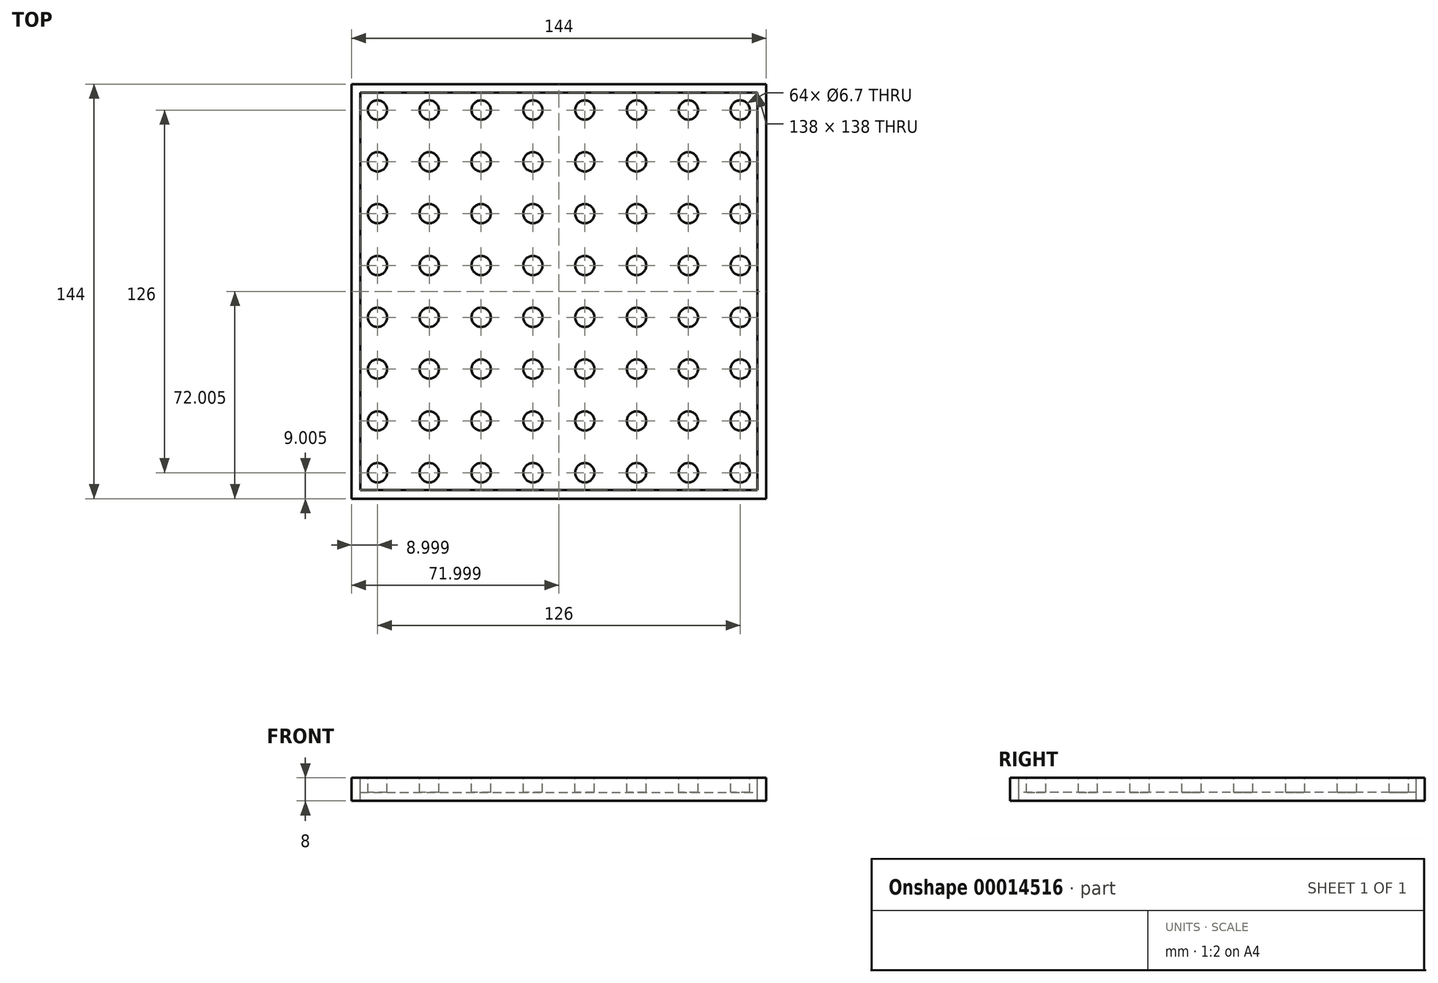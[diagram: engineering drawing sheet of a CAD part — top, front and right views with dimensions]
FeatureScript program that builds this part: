
annotation { "Feature Type Name" : "Feature", "Feature Type Description" : "" }
export const myFeature = defineFeature(function(context is Context, id is Id, definition is map)
    precondition{}
    {
        {
            var Q0;
            Q0=qCreatedBy(makeId("Top.planeOp"),FACE);
            var sketch = newSketch(context, id + "F0", { "sketchPlane" : qUnion([Q0])});
            skLineSegment(sketch, "E0.bottom", {"start": v(-70.46, 51.71) * mm, "end": v(73.54, 51.71) * mm});
            skLineSegment(sketch, "E0.top", {"start": v(-70.46, -92.29) * mm, "end": v(73.54, -92.29) * mm});
            skLineSegment(sketch, "E0.left", {"start": v(-70.46, 51.71) * mm, "end": v(-70.46, -92.29) * mm});
            skLineSegment(sketch, "E0.right", {"start": v(73.54, 51.71) * mm, "end": v(73.54, -92.29) * mm});
            skLineSegment(sketch, "E1.0", {"start": v(-67.46, 48.71) * mm, "end": v(70.54, 48.71) * mm});
            skLineSegment(sketch, "E1.1", {"start": v(-67.46, 48.71) * mm, "end": v(-67.46, -89.29) * mm});
            skLineSegment(sketch, "E1.2", {"start": v(-67.46, -89.29) * mm, "end": v(70.54, -89.29) * mm});
            skLineSegment(sketch, "E1.3", {"start": v(70.54, 48.71) * mm, "end": v(70.54, -89.29) * mm});
            skCircle(sketch, "E2", {"center": v(-61.46, 42.71) * mm, "radius": 3.35 * mm});
            skCircle(sketch, "E3.0.1.0", {"center": v(-61.46, 24.71) * mm, "radius": 3.35 * mm});
            skCircle(sketch, "E3.0.2.0", {"center": v(-61.46, 6.71) * mm, "radius": 3.35 * mm});
            skCircle(sketch, "E3.0.3.0", {"center": v(-61.46, -11.29) * mm, "radius": 3.35 * mm});
            skCircle(sketch, "E3.0.4.0", {"center": v(-61.46, -29.29) * mm, "radius": 3.35 * mm});
            skCircle(sketch, "E3.0.5.0", {"center": v(-61.46, -47.29) * mm, "radius": 3.35 * mm});
            skCircle(sketch, "E3.0.6.0", {"center": v(-61.46, -65.29) * mm, "radius": 3.35 * mm});
            skCircle(sketch, "E3.1.0.0", {"center": v(-43.46, 42.71) * mm, "radius": 3.35 * mm});
            skCircle(sketch, "E3.1.1.0", {"center": v(-43.46, 24.71) * mm, "radius": 3.35 * mm});
            skCircle(sketch, "E3.1.2.0", {"center": v(-43.46, 6.71) * mm, "radius": 3.35 * mm});
            skCircle(sketch, "E3.1.3.0", {"center": v(-43.46, -11.29) * mm, "radius": 3.35 * mm});
            skCircle(sketch, "E3.1.4.0", {"center": v(-43.46, -29.29) * mm, "radius": 3.35 * mm});
            skCircle(sketch, "E3.1.5.0", {"center": v(-43.46, -47.29) * mm, "radius": 3.35 * mm});
            skCircle(sketch, "E3.1.6.0", {"center": v(-43.46, -65.29) * mm, "radius": 3.35 * mm});
            skCircle(sketch, "E3.2.0.0", {"center": v(-25.46, 42.71) * mm, "radius": 3.35 * mm});
            skCircle(sketch, "E3.2.1.0", {"center": v(-25.46, 24.71) * mm, "radius": 3.35 * mm});
            skCircle(sketch, "E3.2.2.0", {"center": v(-25.46, 6.71) * mm, "radius": 3.35 * mm});
            skCircle(sketch, "E3.2.3.0", {"center": v(-25.46, -11.29) * mm, "radius": 3.35 * mm});
            skCircle(sketch, "E3.2.4.0", {"center": v(-25.46, -29.29) * mm, "radius": 3.35 * mm});
            skCircle(sketch, "E3.2.5.0", {"center": v(-25.46, -47.29) * mm, "radius": 3.35 * mm});
            skCircle(sketch, "E3.2.6.0", {"center": v(-25.46, -65.29) * mm, "radius": 3.35 * mm});
            skCircle(sketch, "E3.3.0.0", {"center": v(-7.46, 42.71) * mm, "radius": 3.35 * mm});
            skCircle(sketch, "E3.3.1.0", {"center": v(-7.46, 24.71) * mm, "radius": 3.35 * mm});
            skCircle(sketch, "E3.3.2.0", {"center": v(-7.46, 6.71) * mm, "radius": 3.35 * mm});
            skCircle(sketch, "E3.3.3.0", {"center": v(-7.46, -11.29) * mm, "radius": 3.35 * mm});
            skCircle(sketch, "E3.3.4.0", {"center": v(-7.46, -29.29) * mm, "radius": 3.35 * mm});
            skCircle(sketch, "E3.3.5.0", {"center": v(-7.46, -47.29) * mm, "radius": 3.35 * mm});
            skCircle(sketch, "E3.3.6.0", {"center": v(-7.46, -65.29) * mm, "radius": 3.35 * mm});
            skCircle(sketch, "E3.4.0.0", {"center": v(10.54, 42.71) * mm, "radius": 3.35 * mm});
            skCircle(sketch, "E3.4.1.0", {"center": v(10.54, 24.71) * mm, "radius": 3.35 * mm});
            skCircle(sketch, "E3.4.2.0", {"center": v(10.54, 6.71) * mm, "radius": 3.35 * mm});
            skCircle(sketch, "E3.4.3.0", {"center": v(10.54, -11.29) * mm, "radius": 3.35 * mm});
            skCircle(sketch, "E3.4.4.0", {"center": v(10.54, -29.29) * mm, "radius": 3.35 * mm});
            skCircle(sketch, "E3.4.5.0", {"center": v(10.54, -47.29) * mm, "radius": 3.35 * mm});
            skCircle(sketch, "E3.4.6.0", {"center": v(10.54, -65.29) * mm, "radius": 3.35 * mm});
            skCircle(sketch, "E3.5.0.0", {"center": v(28.54, 42.71) * mm, "radius": 3.35 * mm});
            skCircle(sketch, "E3.5.1.0", {"center": v(28.54, 24.71) * mm, "radius": 3.35 * mm});
            skCircle(sketch, "E3.5.2.0", {"center": v(28.54, 6.71) * mm, "radius": 3.35 * mm});
            skCircle(sketch, "E3.5.3.0", {"center": v(28.54, -11.29) * mm, "radius": 3.35 * mm});
            skCircle(sketch, "E3.5.4.0", {"center": v(28.54, -29.29) * mm, "radius": 3.35 * mm});
            skCircle(sketch, "E3.5.5.0", {"center": v(28.54, -47.29) * mm, "radius": 3.35 * mm});
            skCircle(sketch, "E3.5.6.0", {"center": v(28.54, -65.29) * mm, "radius": 3.35 * mm});
            skCircle(sketch, "E3.6.0.0", {"center": v(46.54, 42.71) * mm, "radius": 3.35 * mm});
            skCircle(sketch, "E3.6.1.0", {"center": v(46.54, 24.71) * mm, "radius": 3.35 * mm});
            skCircle(sketch, "E3.6.2.0", {"center": v(46.54, 6.71) * mm, "radius": 3.35 * mm});
            skCircle(sketch, "E3.6.3.0", {"center": v(46.54, -11.29) * mm, "radius": 3.35 * mm});
            skCircle(sketch, "E3.6.4.0", {"center": v(46.54, -29.29) * mm, "radius": 3.35 * mm});
            skCircle(sketch, "E3.6.5.0", {"center": v(46.54, -47.29) * mm, "radius": 3.35 * mm});
            skCircle(sketch, "E3.6.6.0", {"center": v(46.54, -65.29) * mm, "radius": 3.35 * mm});
            skLineSegment(sketch, "E3.direction1", {"start": v(-61.46, 42.71) * mm, "end": v(-43.46, 42.71) * mm, "construction": true});
            skLineSegment(sketch, "E3.direction2", {"start": v(-61.46, 42.71) * mm, "end": v(-61.46, 24.71) * mm, "construction": true});
            skCircle(sketch, "E4.0.0.7", {"center": v(-61.46, -83.29) * mm, "radius": 3.35 * mm});
            skCircle(sketch, "E4.0.1.7", {"center": v(-43.46, -83.29) * mm, "radius": 3.35 * mm});
            skCircle(sketch, "E4.0.2.7", {"center": v(-25.46, -83.29) * mm, "radius": 3.35 * mm});
            skCircle(sketch, "E4.0.3.7", {"center": v(-7.46, -83.29) * mm, "radius": 3.35 * mm});
            skCircle(sketch, "E4.0.4.7", {"center": v(10.54, -83.29) * mm, "radius": 3.35 * mm});
            skCircle(sketch, "E4.0.5.7", {"center": v(28.54, -83.29) * mm, "radius": 3.35 * mm});
            skCircle(sketch, "E4.0.6.7", {"center": v(46.54, -83.29) * mm, "radius": 3.35 * mm});
            skCircle(sketch, "E5.0.7.0", {"center": v(64.54, 42.71) * mm, "radius": 3.35 * mm});
            skCircle(sketch, "E5.0.7.1", {"center": v(64.54, 24.71) * mm, "radius": 3.35 * mm});
            skCircle(sketch, "E5.0.7.2", {"center": v(64.54, 6.71) * mm, "radius": 3.35 * mm});
            skCircle(sketch, "E5.0.7.3", {"center": v(64.54, -11.29) * mm, "radius": 3.35 * mm});
            skCircle(sketch, "E5.0.7.4", {"center": v(64.54, -29.29) * mm, "radius": 3.35 * mm});
            skCircle(sketch, "E5.0.7.5", {"center": v(64.54, -47.29) * mm, "radius": 3.35 * mm});
            skCircle(sketch, "E5.0.7.6", {"center": v(64.54, -65.29) * mm, "radius": 3.35 * mm});
            skCircle(sketch, "E5.0.7.7", {"center": v(64.54, -83.29) * mm, "radius": 3.35 * mm});
            skSolve(sketch);
        }
        {
            var Q0;
            Q0=makeQuery(id+"F0.imprint","IMPRINT",FACE,{"disambiguationData":[TD([[makeQuery(id+"F0.imprint","IMPRINT",EDGE,{"derivedFrom":sQuery(id+"F0.wireOp",EDGE,"E1.0")}),-1.0]])]});
            extrude(context, id + "F1", {"entities" : qUnion([Q0]), "oppositeDirection" : true, "depth" : 5 * mm});
        }
        {
            var Q0;
            Q0=makeQuery(id+"F0.imprint","IMPRINT",FACE,{"disambiguationData":[TD([[makeQuery(id+"F0.imprint","IMPRINT",EDGE,{"derivedFrom":sQuery(id+"F0.wireOp",EDGE,"E0.bottom")}),-1.0]])]});
            extrude(context, id + "F2", {"entities" : qUnion([Q0]), "oppositeDirection" : true, "depth" : 8 * mm});
        }
    });
